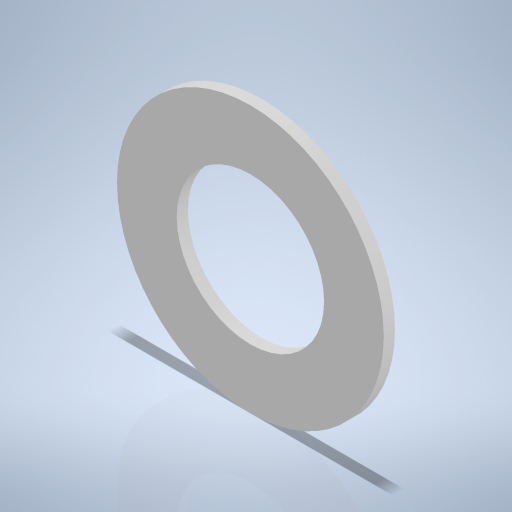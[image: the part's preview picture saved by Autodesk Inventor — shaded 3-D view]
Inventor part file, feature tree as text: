
AUTODESK INVENTOR PART (.ipt)
format: ipt  version: 2024 (Build 280153000, 153)  size: 227,328 bytes
history: native  units: mm
features: extrude x1, sketch x1
ambient origin geometry x8: Origin, YZ Plane, XZ Plane, XY Plane, X Axis, Y Axis, Z Axis, Center Point
bodies: Volumenkörper1 (feature_tree)
feature tree (2):
  extrude  "Extrusion1"  Depth=0.8mm
  sketch  "Skizze1"  dims[d0=19.0mm d1=10.5mm d2=0.8mm d3=0.0mm]
